# Revit family: CWSS-RW-S6 ENScape optisk-akustisk signalgiver rød_Vegg
name_source: partatom
category: Fire Alarm Devices
revit_build: Autodesk Revit 2016 (Build: 20160314_0715(x64)
units: mm (PartAtom-declared; Revit-internal decimal feet)

## family parameters
Always vertical = No
Cut with Voids When Loaded = No
Maintain Annotation Orientation = Yes
OmniClass Number = 23.85.30.21.14.11
OmniClass Title = Concentration Detection Bells and Sounders
Part Type = Normal
Room Calculation Point = No
Round Connector Dimension = Use Diameter
Shared = No
Work Plane-Based = No

## types (1)
- Akustisk signalgiver
    Assembly Code = 5423
    CQ Length A = 100 mm  [stored 0.328084 ft]
    CQ Length B = 98 mm  [stored 0.321522 ft]
    CQ Material = Plastic - Red
    Keynote = XN1
    Manufacturer = Honeywell
    NS8360 = 5423_XN1
    Type Comments = -XH

note: [stored X ft] marks values corroborated as IEEE doubles in the binary element streams (Revit-internal decimal feet)

## geometry (parser evidence)
native form markers: Blend x2, Sweep x3
no freeform markers — native parametric forms only
